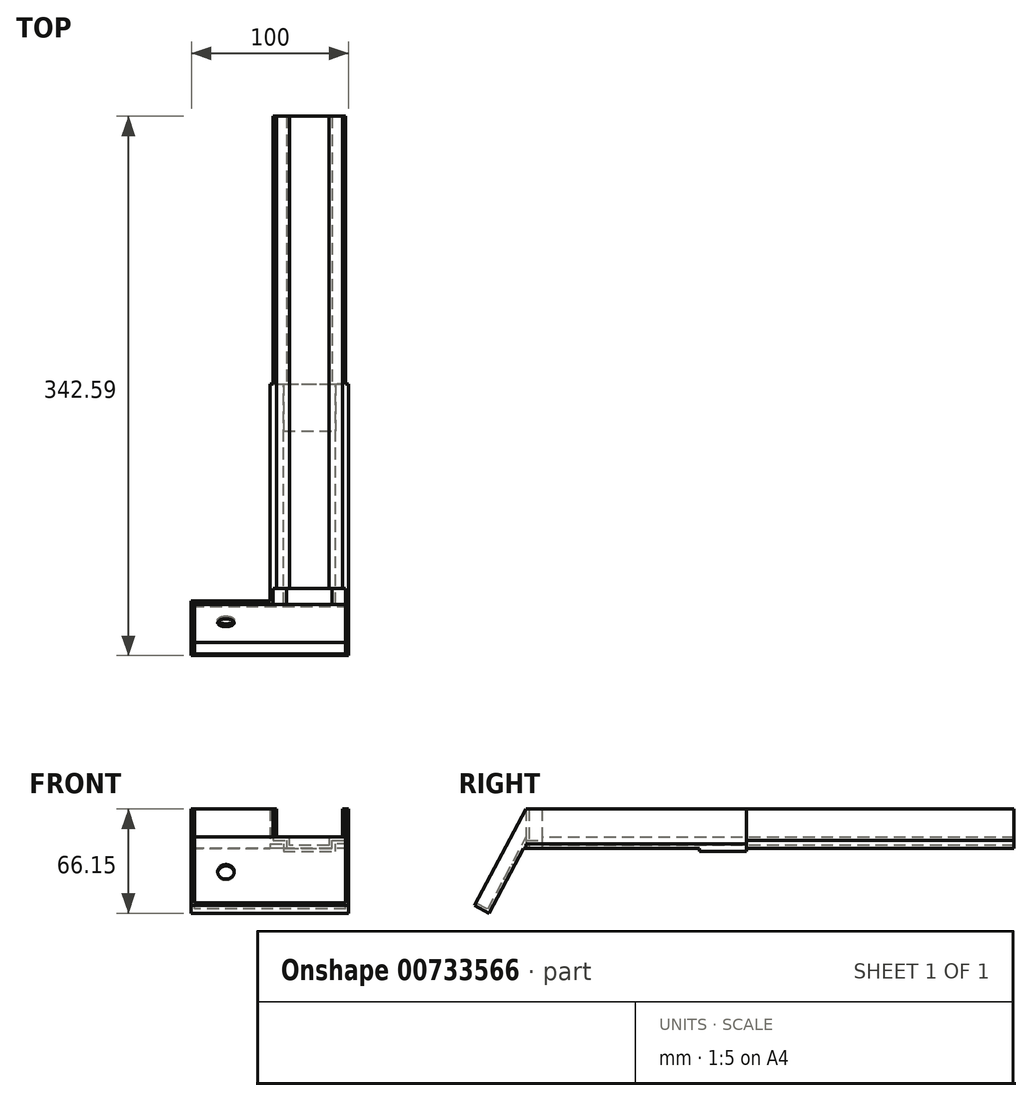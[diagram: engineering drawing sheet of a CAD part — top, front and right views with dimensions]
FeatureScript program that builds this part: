
annotation { "Feature Type Name" : "Feature", "Feature Type Description" : "" }
export const myFeature = defineFeature(function(context is Context, id is Id, definition is map)
    precondition{}
    {
        {
            var Q0;
            Q0=qCreatedBy(makeId("Front.planeOp"),FACE);
            var sketch = newSketch(context, id + "F0", { "sketchPlane" : qUnion([Q0])});
            skLineSegment(sketch, "E0", {"start": v(-45.71, 45.04) * mm, "end": v(-45.71, 25.04) * mm});
            skLineSegment(sketch, "E1", {"start": v(-45.71, 25.04) * mm, "end": v(-37.21, 25.04) * mm});
            skLineSegment(sketch, "E2", {"start": v(-37.21, 25.04) * mm, "end": v(-37.21, 20.04) * mm});
            skLineSegment(sketch, "E3", {"start": v(-37.21, 20.04) * mm, "end": v(-8.21, 20.04) * mm});
            skLineSegment(sketch, "E4", {"start": v(-8.21, 20.04) * mm, "end": v(-8.21, 25.04) * mm});
            skLineSegment(sketch, "E5", {"start": v(-8.21, 25.04) * mm, "end": v(0.29, 25.04) * mm});
            skLineSegment(sketch, "E6", {"start": v(0.29, 25.04) * mm, "end": v(0.29, 45.04) * mm});
            skLineSegment(sketch, "E7", {"start": v(0.29, 45.04) * mm, "end": v(-1.71, 45.04) * mm});
            skLineSegment(sketch, "E8", {"start": v(-1.71, 45.04) * mm, "end": v(-1.71, 27.04) * mm});
            skLineSegment(sketch, "E9", {"start": v(-1.71, 27.04) * mm, "end": v(-10.21, 27.04) * mm});
            skLineSegment(sketch, "E10", {"start": v(-10.21, 27.04) * mm, "end": v(-10.21, 22.04) * mm});
            skLineSegment(sketch, "E11", {"start": v(-10.21, 22.04) * mm, "end": v(-35.21, 22.04) * mm});
            skLineSegment(sketch, "E12", {"start": v(-35.21, 22.04) * mm, "end": v(-35.21, 27.04) * mm});
            skLineSegment(sketch, "E13", {"start": v(-35.21, 27.04) * mm, "end": v(-43.71, 27.04) * mm});
            skLineSegment(sketch, "E14", {"start": v(-43.71, 27.04) * mm, "end": v(-43.71, 45.04) * mm});
            skLineSegment(sketch, "E15", {"start": v(-43.71, 45.04) * mm, "end": v(-45.71, 45.04) * mm});
            skLineSegment(sketch, "E16", {"start": v(-45.71, 45.04) * mm, "end": v(-47.71, 45.04) * mm});
            skLineSegment(sketch, "E17", {"start": v(-47.71, 45.04) * mm, "end": v(-47.71, 23.04) * mm});
            skLineSegment(sketch, "E18", {"start": v(-47.71, 23.04) * mm, "end": v(-39.21, 23.04) * mm});
            skLineSegment(sketch, "E19", {"start": v(0.29, 45.04) * mm, "end": v(2.29, 45.04) * mm});
            skLineSegment(sketch, "E20", {"start": v(2.29, 45.04) * mm, "end": v(2.29, 23.04) * mm});
            skLineSegment(sketch, "E21", {"start": v(2.29, 23.04) * mm, "end": v(-6.21, 23.04) * mm});
            skLineSegment(sketch, "E22", {"start": v(-39.21, 23.04) * mm, "end": v(-39.21, 18.04) * mm});
            skLineSegment(sketch, "E23", {"start": v(-39.21, 18.04) * mm, "end": v(-6.21, 18.04) * mm});
            skLineSegment(sketch, "E24", {"start": v(-6.21, 18.04) * mm, "end": v(-6.21, 23.04) * mm});
            skLineSegment(sketch, "E25", {"start": v(-37.21, 20.04) * mm, "end": v(-39.21, 20.04) * mm});
            skLineSegment(sketch, "E26", {"start": v(-8.21, 20.04) * mm, "end": v(-6.21, 20.04) * mm});
            skSolve(sketch);
        }
        {
            var Q0;
            Q0=makeQuery(id+"F0.imprint","IMPRINT",FACE,{"disambiguationData":[TD([[makeQuery(id+"F0.imprint","IMPRINT",EDGE,{"derivedFrom":sQuery(id+"F0.wireOp",EDGE,"E0")}),1.0]])]});
            extrude(context, id + "F1", {"entities" : qUnion([Q0]), "oppositeDirection" : true, "depth" : 300 * mm, "offsetDistance" : 25 * mm});
        }
        {
            var Q0;
            Q0=makeQuery(id+"F0.imprint","IMPRINT",FACE,{"disambiguationData":[TD([[makeQuery(id+"F0.imprint","IMPRINT",EDGE,{"derivedFrom":sQuery(id+"F0.wireOp",EDGE,"E0")}),-1.0]])]});
            var Q1;
            Q1=makeQuery(id+"F0.imprint","IMPRINT",FACE,{"disambiguationData":[TD([[makeQuery(id+"F0.imprint","IMPRINT",EDGE,{"derivedFrom":sQuery(id+"F0.wireOp",EDGE,"E4")}),-1.0]])]});
            extrude(context, id + "F2", {"entities" : qUnion([Q0, Q1]), "depth" : 10 * mm, "offsetDistance" : 25 * mm, "hasSecondDirection" : true, "secondDirectionOppositeDirection" : true, "secondDirectionDepth" : 130 * mm});
        }
        {
            var Q0;
            Q0=makeQuery(id+"F2.opExtrude","SWEPT_FACE",FACE,{"disambiguationData":[OSD([sQuery(id+"F0.wireOp",EDGE,"E17")])]});
            var sketch = newSketch(context, id + "F3", { "sketchPlane" : qUnion([Q0])});
            skLineSegment(sketch, "E27", {"start": v(10, 23.04) * mm, "end": v(33.47, -21.1) * mm});
            skLineSegment(sketch, "E28", {"start": v(33.47, -21.1) * mm, "end": v(42.6, -16.26) * mm});
            skLineSegment(sketch, "E29", {"start": v(42.6, -16.26) * mm, "end": v(19.12, 27.9) * mm});
            skLineSegment(sketch, "E30", {"start": v(19.12, 27.9) * mm, "end": v(10, 23.04) * mm});
            skLineSegment(sketch, "E31", {"start": v(19.12, 27.9) * mm, "end": v(10, 45.04) * mm});
            skLineSegment(sketch, "E32", {"start": v(35.24, -20.17) * mm, "end": v(10, 27.3) * mm});
            skLineSegment(sketch, "E33", {"start": v(11.6, 20.04) * mm, "end": v(10, 20.04) * mm});
            skLineSegment(sketch, "E34", {"start": v(10, 23.04) * mm, "end": v(10, 20.04) * mm});
            skLineSegment(sketch, "E35", {"start": v(10, 45.04) * mm, "end": v(8, 45.04) * mm});
            skLineSegment(sketch, "E36", {"start": v(8, 45.04) * mm, "end": v(8, 20.04) * mm});
            skLineSegment(sketch, "E37", {"start": v(8, 20.04) * mm, "end": v(10, 20.04) * mm});
            skLineSegment(sketch, "E38", {"start": v(41.65, -14.5) * mm, "end": v(32.53, -19.34) * mm});
            skSolve(sketch);
        }
        {
            var Q0;
            {var subQ0=sQuery(id+"F3.wireOp",EDGE,"E27");Q0=makeQuery(id+"F3.imprint","IMPRINT",FACE,{"disambiguationData":[TD([[makeQuery(id+"F3.imprint","IMPRINT",EDGE,{"derivedFrom":subQ0}),1.0]])]});}
            var Q1;
            {var subQ1=sQuery(id+"F0.wireOp",EDGE,"E17");var subQ2=makeQuery(id+"F2.opExtrude","CAP_EDGE",EDGE,{"disambiguationData":[OSD([subQ1])],"isStart":false});var subQ4=sQuery(id+"F3.wireOp",EDGE,"E32");var subQ6=makeQuery(id+"F3.imprint","INTERSECT",VERTEX,{"derivedFrom":[subQ2,subQ4]});Q1=makeQuery(id+"F3.imprint","IMPRINT",FACE,{"disambiguationData":[TD([[makeQuery(id+"F3.imprint","IMPRINT",EDGE,{"disambiguationData":[TD([[subQ6,1.0]])],"derivedFrom":subQ4}),1.0]])]});}
            var Q2;
            {var subQ3=sQuery(id+"F3.wireOp",EDGE,"E33");Q2=makeQuery(id+"F3.imprint","IMPRINT",FACE,{"disambiguationData":[TD([[makeQuery(id+"F3.imprint","IMPRINT",EDGE,{"derivedFrom":subQ3}),-1.0]])]});}
            extrude(context, id + "F4", {"entities" : qUnion([Q0, Q1, Q2]), "operationType" : NewBodyOperationType.ADD, "oppositeDirection" : true, "depth" : 50 * mm, "offsetDistance" : 25 * mm, "hasSecondDirection" : true, "secondDirectionOppositeDirection" : false, "secondDirectionDepth" : 50 * mm});
        }
        {
            var Q0;
            {var subQ0=sQuery(id+"F3.wireOp",EDGE,"E30");var subQ5=sQuery(id+"F3.wireOp",EDGE,"E32");var subQ6=makeQuery(id+"F3.imprint","INTERSECT",VERTEX,{"derivedFrom":[subQ0,subQ5]});Q0=makeQuery(id+"F3.imprint","IMPRINT",FACE,{"disambiguationData":[TD([[makeQuery(id+"F3.imprint","IMPRINT",EDGE,{"disambiguationData":[TD([[subQ6,1.0]])],"derivedFrom":subQ5}),-1.0]])]});}
            var Q1;
            {var subQ0=sQuery(id+"F3.wireOp",EDGE,"E31");Q1=makeQuery(id+"F3.imprint","IMPRINT",FACE,{"disambiguationData":[TD([[makeQuery(id+"F3.imprint","IMPRINT",EDGE,{"derivedFrom":subQ0}),1.0]])]});}
            extrude(context, id + "F5", {"entities" : qUnion([Q0, Q1]), "operationType" : NewBodyOperationType.ADD, "oppositeDirection" : true, "depth" : 50 * mm, "offsetDistance" : 25 * mm, "hasSecondDirection" : true, "secondDirectionOppositeDirection" : true, "secondDirectionDepth" : 48 * mm});
        }
        {
            var Q0;
            Q0=makeQuery(id+"F0.imprint","IMPRINT",FACE,{"disambiguationData":[TD([[makeQuery(id+"F0.imprint","IMPRINT",EDGE,{"derivedFrom":sQuery(id+"F0.wireOp",EDGE,"E3")}),-1.0]])]});
            extrude(context, id + "F6", {"entities" : qUnion([Q0]), "operationType" : NewBodyOperationType.ADD, "oppositeDirection" : true, "depth" : 130 * mm, "offsetDistance" : 25 * mm, "hasSecondDirection" : true, "secondDirectionOppositeDirection" : true, "secondDirectionDepth" : 100 * mm});
        }
        {
            var Q0;
            Q0=makeQuery(id+"F4.opExtrude","SWEPT_FACE",FACE,{"disambiguationData":[OSD([sQuery(id+"F3.wireOp",EDGE,"E32")])]});
            var sketch = newSketch(context, id + "F7", { "sketchPlane" : qUnion([Q0])});
            skCircle(sketch, "E39", {"center": v(-75.71, -5.59) * mm, "radius": 5.25 * mm});
            skSolve(sketch);
        }
        {
            var Q0;
            {var subQ0=sQuery(id+"F3.wireOp",EDGE,"E30");var subQ5=sQuery(id+"F3.wireOp",EDGE,"E32");var subQ6=makeQuery(id+"F3.imprint","INTERSECT",VERTEX,{"derivedFrom":[subQ0,subQ5]});Q0=makeQuery(id+"F3.imprint","IMPRINT",FACE,{"disambiguationData":[TD([[makeQuery(id+"F3.imprint","IMPRINT",EDGE,{"disambiguationData":[TD([[subQ6,1.0]])],"derivedFrom":subQ5}),-1.0]])]});}
            var Q1;
            {var subQ0=sQuery(id+"F3.wireOp",EDGE,"E31");Q1=makeQuery(id+"F3.imprint","IMPRINT",FACE,{"disambiguationData":[TD([[makeQuery(id+"F3.imprint","IMPRINT",EDGE,{"derivedFrom":subQ0}),1.0]])]});}
            extrude(context, id + "F8", {"entities" : qUnion([Q0, Q1]), "operationType" : NewBodyOperationType.ADD, "depth" : 50 * mm, "offsetDistance" : 25 * mm, "hasSecondDirection" : true, "secondDirectionOppositeDirection" : false, "secondDirectionDepth" : 48 * mm});
        }
        {
            var Q0;
            {var subQ0=sQuery(id+"F3.wireOp",EDGE,"E35");Q0=makeQuery(id+"F3.imprint","IMPRINT",FACE,{"disambiguationData":[TD([[makeQuery(id+"F3.imprint","IMPRINT",EDGE,{"derivedFrom":subQ0}),1.0]])]});}
            var Q1;
            {var subQ0=sQuery(id+"F3.wireOp",EDGE,"E34");Q1=makeQuery(id+"F3.imprint","IMPRINT",FACE,{"disambiguationData":[TD([[makeQuery(id+"F3.imprint","IMPRINT",EDGE,{"derivedFrom":subQ0}),-1.0]])]});}
            extrude(context, id + "F9", {"entities" : qUnion([Q0, Q1]), "operationType" : NewBodyOperationType.ADD, "depth" : 50 * mm, "offsetDistance" : 25 * mm});
        }
        {
            var Q0;
            {var subQ0=sQuery(id+"F3.wireOp",EDGE,"E28");var subQ1=sQuery(id+"F3.wireOp",EDGE,"E27");var subQ2=makeQuery(id+"F3.imprint","INTERSECT",VERTEX,{"derivedFrom":[subQ1,subQ0]});Q0=makeQuery(id+"F3.imprint","IMPRINT",FACE,{"disambiguationData":[TD([[makeQuery(id+"F3.imprint","IMPRINT",EDGE,{"disambiguationData":[TD([[subQ2,1.0]])],"derivedFrom":subQ1}),1.0]])]});}
            var Q1;
            {var subQ0=sQuery(id+"F3.wireOp",EDGE,"E29");var subQ1=sQuery(id+"F3.wireOp",EDGE,"E28");var subQ2=makeQuery(id+"F3.imprint","INTERSECT",VERTEX,{"derivedFrom":[subQ1,subQ0]});Q1=makeQuery(id+"F3.imprint","IMPRINT",FACE,{"disambiguationData":[TD([[makeQuery(id+"F3.imprint","IMPRINT",EDGE,{"disambiguationData":[TD([[subQ2,1.0]])],"derivedFrom":subQ1}),1.0]])]});}
            extrude(context, id + "F10", {"entities" : qUnion([Q0, Q1]), "operationType" : NewBodyOperationType.ADD, "depth" : 50 * mm, "offsetDistance" : 25 * mm, "hasSecondDirection" : true, "secondDirectionOppositeDirection" : true, "secondDirectionDepth" : 50 * mm});
        }
        {
            var Q0;
            Q0=makeQuery(id+"F7.imprint","IMPRINT",FACE,{"disambiguationData":[TD([[makeQuery(id+"F7.imprint","IMPRINT",EDGE,{"derivedFrom":sQuery(id+"F7.wireOp",EDGE,"E39")}),1.0]])]});
            extrude(context, id + "F11", {"entities" : qUnion([Q0]), "operationType" : NewBodyOperationType.REMOVE, "oppositeDirection" : true, "depth" : 25 * mm, "offsetDistance" : 25 * mm});
        }
    });
